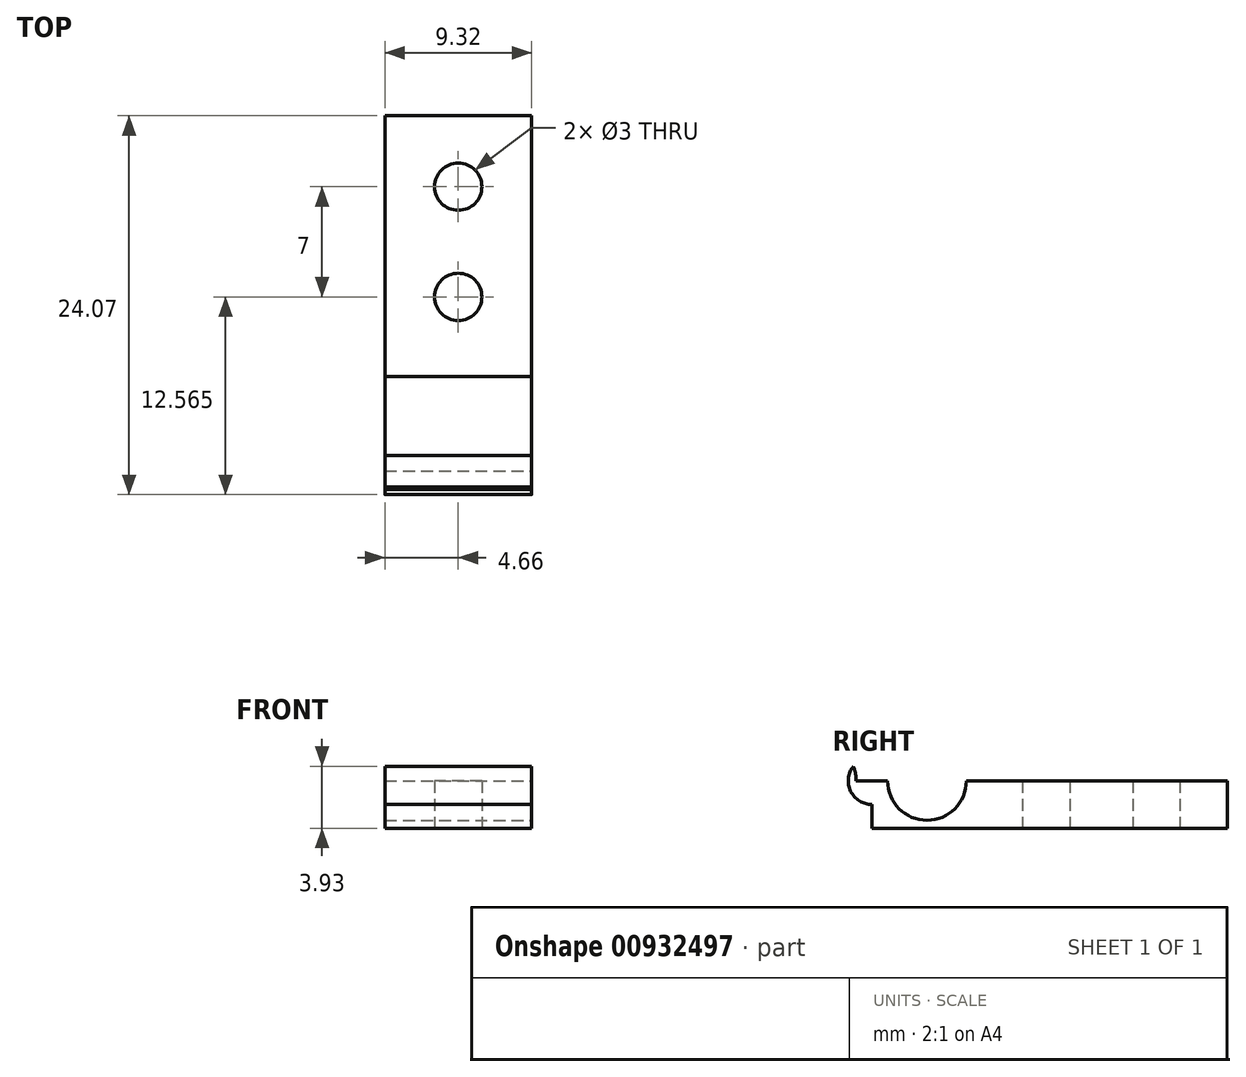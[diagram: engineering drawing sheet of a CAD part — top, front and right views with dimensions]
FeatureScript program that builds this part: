
annotation { "Feature Type Name" : "Feature", "Feature Type Description" : "" }
export const myFeature = defineFeature(function(context is Context, id is Id, definition is map)
    precondition{}
    {
        {
            var Q0;
            Q0=qCreatedBy(makeId("Top.planeOp"),FACE);
            var sketch = newSketch(context, id + "F0", { "sketchPlane" : qUnion([Q0])});
            skLineSegment(sketch, "E0.bottom", {"start": v(4.66, 22.57) * mm, "end": v(-4.66, 22.57) * mm});
            skLineSegment(sketch, "E0.top", {"start": v(4.66, -22.57) * mm, "end": v(-4.66, -22.57) * mm});
            skLineSegment(sketch, "E0.left", {"start": v(4.66, 22.57) * mm, "end": v(4.66, -22.57) * mm});
            skLineSegment(sketch, "E0.right", {"start": v(-4.66, 22.57) * mm, "end": v(-4.66, -22.57) * mm});
            skPoint(sketch, "E0.middle", {"position": v(0, 0) * mm});
            skLineSegment(sketch, "E1", {"start": v(0, 22.57) * mm, "end": v(0, -22.57) * mm, "construction": true});
            skLineSegment(sketch, "E2", {"start": v(4.66, 0) * mm, "end": v(-4.66, 0) * mm, "construction": true});
            skCircle(sketch, "E3", {"center": v(0, 18.07) * mm, "radius": 1.5 * mm});
            skCircle(sketch, "E4", {"center": v(0, 11.07) * mm, "radius": 1.5 * mm});
            skCircle(sketch, "E5.MirrorC", {"center": v(0, -11.07) * mm, "radius": 1.5 * mm});
            skCircle(sketch, "E6.MirrorC", {"center": v(0, -18.07) * mm, "radius": 1.5 * mm});
            skSolve(sketch);
        }
        {
            var Q0;
            Q0=makeQuery(id+"F0.imprint","IMPRINT",FACE,{"disambiguationData":[TD([[makeQuery(id+"F0.imprint","IMPRINT",EDGE,{"derivedFrom":sQuery(id+"F0.wireOp",EDGE,"E0.bottom")}),1.0]])]});
            extrude(context, id + "F1", {"entities" : qUnion([Q0]), "depth" : 6 * mm, "offsetDistance" : 25 * mm});
        }
        {
            var Q0;
            Q0=makeQuery(id+"F1.opExtrude","SWEPT_FACE",FACE,{"disambiguationData":[OSD([sQuery(id+"F0.wireOp",EDGE,"E0.left")])]});
            var sketch = newSketch(context, id + "F2", { "sketchPlane" : qUnion([Q0])});
            skLineSegment(sketch, "E7", {"start": v(0, 0) * mm, "end": v(0, 6) * mm});
            skLineSegment(sketch, "E8", {"start": v(22.57, 3) * mm, "end": v(-22.57, 3) * mm});
            skCircle(sketch, "E9", {"center": v(0, 3) * mm, "radius": 1.5 * mm});
            skCircle(sketch, "E10", {"center": v(3.5, 3) * mm, "radius": 2.5 * mm});
            skCircle(sketch, "E11.MirrorC", {"center": v(-3.5, 3) * mm, "radius": 2.5 * mm});
            skSolve(sketch);
        }
        {
            var Q0;
            {var subQ0=sQuery(id+"F2.wireOp",EDGE,"E10");var subQ1=sQuery(id+"F2.wireOp",EDGE,"E8");var subQ2=makeQuery(id+"F2.imprint","INTERSECT",VERTEX,{"disambiguationData":[OD(0.0)],"derivedFrom":[subQ1,subQ0]});Q0=makeQuery(id+"F2.imprint","IMPRINT",FACE,{"disambiguationData":[TD([[makeQuery(id+"F2.imprint","IMPRINT",EDGE,{"disambiguationData":[TD([[subQ2,-1.0]])],"derivedFrom":subQ1}),-1.0]])]});}
            var Q1;
            {var subQ0=sQuery(id+"F2.wireOp",EDGE,"E10");var subQ1=sQuery(id+"F2.wireOp",EDGE,"E8");var subQ2=makeQuery(id+"F2.imprint","INTERSECT",VERTEX,{"disambiguationData":[OD(0.0)],"derivedFrom":[subQ1,subQ0]});Q1=makeQuery(id+"F2.imprint","IMPRINT",FACE,{"disambiguationData":[TD([[makeQuery(id+"F2.imprint","IMPRINT",EDGE,{"disambiguationData":[TD([[subQ2,-1.0]])],"derivedFrom":subQ1}),1.0]])]});}
            var Q2;
            {var subQ0=sQuery(id+"F2.wireOp",EDGE,"E9");var subQ1=sQuery(id+"F2.wireOp",EDGE,"E8");var subQ2=makeQuery(id+"F2.imprint","INTERSECT",VERTEX,{"disambiguationData":[OD(1.0)],"derivedFrom":[subQ1,subQ0]});Q2=makeQuery(id+"F2.imprint","IMPRINT",FACE,{"disambiguationData":[TD([[makeQuery(id+"F2.imprint","IMPRINT",EDGE,{"disambiguationData":[TD([[subQ2,-1.0]])],"derivedFrom":subQ1}),-1.0]])]});}
            var Q3;
            {var subQ0=sQuery(id+"F2.wireOp",EDGE,"E9");var subQ1=sQuery(id+"F2.wireOp",EDGE,"E8");var subQ2=makeQuery(id+"F2.imprint","INTERSECT",VERTEX,{"disambiguationData":[OD(1.0)],"derivedFrom":[subQ1,subQ0]});Q3=makeQuery(id+"F2.imprint","IMPRINT",FACE,{"disambiguationData":[TD([[makeQuery(id+"F2.imprint","IMPRINT",EDGE,{"disambiguationData":[TD([[subQ2,-1.0]])],"derivedFrom":subQ1}),1.0]])]});}
            var Q4;
            {var subQ0=sQuery(id+"F2.wireOp",EDGE,"E11.MirrorC");var subQ1=sQuery(id+"F2.wireOp",EDGE,"E8");var subQ2=makeQuery(id+"F2.imprint","INTERSECT",VERTEX,{"disambiguationData":[OD(0.0)],"derivedFrom":[subQ1,subQ0]});Q4=makeQuery(id+"F2.imprint","IMPRINT",FACE,{"disambiguationData":[TD([[makeQuery(id+"F2.imprint","IMPRINT",EDGE,{"disambiguationData":[TD([[subQ2,-1.0]])],"derivedFrom":subQ1}),-1.0]])]});}
            var Q5;
            {var subQ0=sQuery(id+"F2.wireOp",EDGE,"E11.MirrorC");var subQ1=sQuery(id+"F2.wireOp",EDGE,"E8");var subQ2=makeQuery(id+"F2.imprint","INTERSECT",VERTEX,{"disambiguationData":[OD(0.0)],"derivedFrom":[subQ1,subQ0]});Q5=makeQuery(id+"F2.imprint","IMPRINT",FACE,{"disambiguationData":[TD([[makeQuery(id+"F2.imprint","IMPRINT",EDGE,{"disambiguationData":[TD([[subQ2,-1.0]])],"derivedFrom":subQ1}),1.0]])]});}
            var Q6;
            {var subQ0=sQuery(id+"F2.wireOp",EDGE,"E8");var subQ1=sQuery(id+"F2.wireOp",EDGE,"E7");var subQ2=makeQuery(id+"F2.imprint","INTERSECT",VERTEX,{"derivedFrom":[subQ1,subQ0]});Q6=makeQuery(id+"F2.imprint","IMPRINT",FACE,{"disambiguationData":[TD([[makeQuery(id+"F2.imprint","IMPRINT",EDGE,{"disambiguationData":[TD([[subQ2,-1.0]])],"derivedFrom":subQ1}),1.0]])]});}
            var Q7;
            {var subQ0=sQuery(id+"F2.wireOp",EDGE,"E8");var subQ1=sQuery(id+"F2.wireOp",EDGE,"E7");var subQ2=makeQuery(id+"F2.imprint","INTERSECT",VERTEX,{"derivedFrom":[subQ1,subQ0]});Q7=makeQuery(id+"F2.imprint","IMPRINT",FACE,{"disambiguationData":[TD([[makeQuery(id+"F2.imprint","IMPRINT",EDGE,{"disambiguationData":[TD([[subQ2,-1.0]])],"derivedFrom":subQ1}),-1.0]])]});}
            var Q8;
            {var subQ0=sQuery(id+"F2.wireOp",EDGE,"E9");var subQ1=sQuery(id+"F2.wireOp",EDGE,"E8");var subQ2=makeQuery(id+"F2.imprint","INTERSECT",VERTEX,{"disambiguationData":[OD(0.0)],"derivedFrom":[subQ1,subQ0]});Q8=makeQuery(id+"F2.imprint","IMPRINT",FACE,{"disambiguationData":[TD([[makeQuery(id+"F2.imprint","IMPRINT",EDGE,{"disambiguationData":[TD([[subQ2,-1.0]])],"derivedFrom":subQ1}),-1.0]])]});}
            var Q9;
            {var subQ0=sQuery(id+"F2.wireOp",EDGE,"E9");var subQ1=sQuery(id+"F2.wireOp",EDGE,"E8");var subQ2=makeQuery(id+"F2.imprint","INTERSECT",VERTEX,{"disambiguationData":[OD(0.0)],"derivedFrom":[subQ1,subQ0]});Q9=makeQuery(id+"F2.imprint","IMPRINT",FACE,{"disambiguationData":[TD([[makeQuery(id+"F2.imprint","IMPRINT",EDGE,{"disambiguationData":[TD([[subQ2,-1.0]])],"derivedFrom":subQ1}),1.0]])]});}
            var Q10;
            {var subQ0=sQuery(id+"F2.wireOp",EDGE,"E9");var subQ1=sQuery(id+"F2.wireOp",EDGE,"E7");var subQ2=makeQuery(id+"F2.imprint","INTERSECT",VERTEX,{"disambiguationData":[OD(0.0)],"derivedFrom":[subQ1,subQ0]});Q10=makeQuery(id+"F2.imprint","IMPRINT",FACE,{"disambiguationData":[TD([[makeQuery(id+"F2.imprint","IMPRINT",EDGE,{"disambiguationData":[TD([[subQ2,-1.0]])],"derivedFrom":subQ1}),-1.0]])]});}
            var Q11;
            {var subQ0=sQuery(id+"F2.wireOp",EDGE,"E9");var subQ1=sQuery(id+"F2.wireOp",EDGE,"E7");var subQ2=makeQuery(id+"F2.imprint","INTERSECT",VERTEX,{"disambiguationData":[OD(0.0)],"derivedFrom":[subQ1,subQ0]});Q11=makeQuery(id+"F2.imprint","IMPRINT",FACE,{"disambiguationData":[TD([[makeQuery(id+"F2.imprint","IMPRINT",EDGE,{"disambiguationData":[TD([[subQ2,-1.0]])],"derivedFrom":subQ1}),1.0]])]});}
            extrude(context, id + "F3", {"entities" : qUnion([Q0, Q1, Q2, Q3, Q4, Q5, Q6, Q7, Q8, Q9, Q10, Q11]), "operationType" : NewBodyOperationType.REMOVE, "endBound" : BoundingType.UP_TO_NEXT, "oppositeDirection" : true, "depth" : 25 * mm, "offsetDistance" : 25 * mm});
        }
    });
